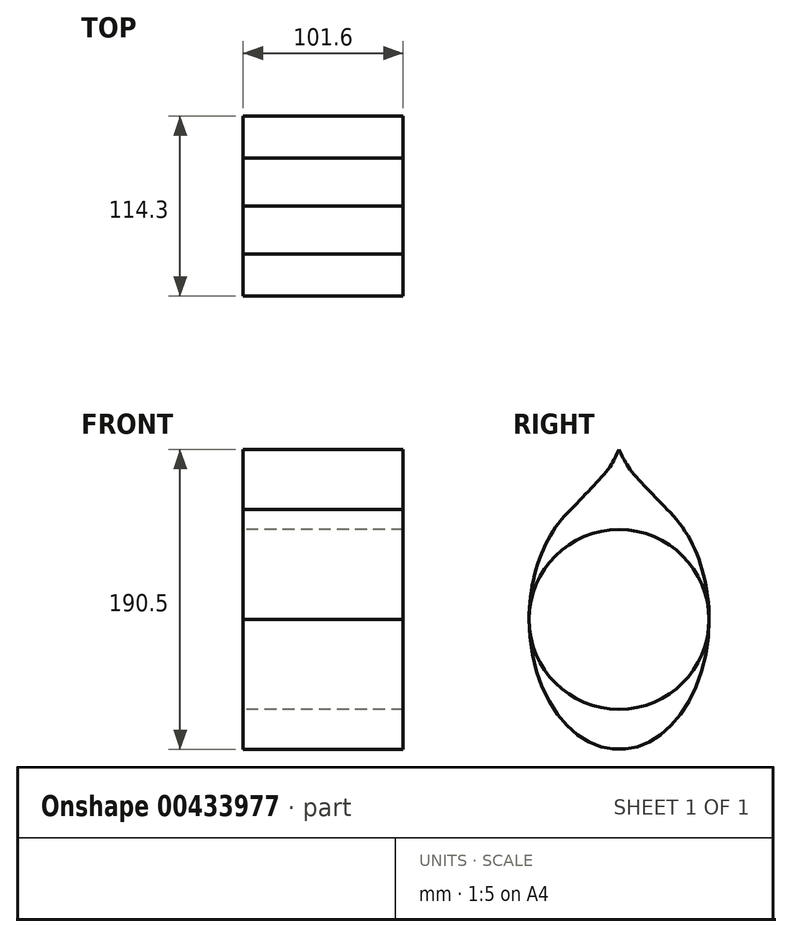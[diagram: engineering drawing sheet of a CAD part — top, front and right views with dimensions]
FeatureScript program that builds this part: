
annotation { "Feature Type Name" : "Feature", "Feature Type Description" : "" }
export const myFeature = defineFeature(function(context is Context, id is Id, definition is map)
    precondition{}
    {
        {
            var Q0;
            Q0=qCreatedBy(makeId("Right.planeOp"),FACE);
            var sketch = newSketch(context, id + "F0", { "sketchPlane" : qUnion([Q0])});
            skCircle(sketch, "E0", {"center": v(0, 0) * mm, "radius": 57.15 * mm});
            skEllipticalArc(sketch, "E1", {});
            skLineSegment(sketch, "E2", {"start": v(0, 82.55) * mm, "end": v(0, 107.95) * mm, "construction": true});
            skLineSegment(sketch, "E3", {"start": v(0, 82.55) * mm, "end": v(0, 57.15) * mm, "construction": true});
            skPoint(sketch, "E4.0.internal.snap0", {"position": v(0, 69.85) * mm});
            skPoint(sketch, "E4.1.internal.snap0", {"position": v(0, 95.25) * mm});
            skFitSpline(sketch, "E4", {"points": [v(30.46, 69.85) * mm, v(7.1, 95.25) * mm, v(0, 107.95) * mm], "startDerivative": vector(-40.1, 45.42) * mm, "endDerivative": vector(-14.34, 29.73) * mm});
            skFitSpline(sketch, "E5.MirrorCS", {"points": [v(-30.46, 69.85) * mm, v(-7.1, 95.25) * mm, v(0, 107.95) * mm], "startDerivative": vector(40.1, 45.42) * mm, "endDerivative": vector(14.34, 29.73) * mm});
            const initialGuessF0  = {"E1": [0, 0, 0, 1, 0.08255, 0.05715, 0.562069803005627, 5.721115504173959]};
            skSetInitialGuess(sketch, initialGuessF0);
            skSolve(sketch);
        }
        {
            var Q0;
            {var subQ0=sQuery(id+"F0.wireOp",EDGE,"E4");Q0=makeQuery(id+"F0.imprint","IMPRINT",FACE,{"disambiguationData":[TD([[makeQuery(id+"F0.imprint","IMPRINT",EDGE,{"derivedFrom":subQ0}),1.0]])]});}
            var Q1;
            {var subQ0=sQuery(id+"F0.wireOp",EDGE,"E1");var subQ1=sQuery(id+"F0.wireOp",EDGE,"E0");var subQ2=makeQuery(id+"F0.imprint","INTERSECT",VERTEX,{"disambiguationData":[OD(0.0)],"derivedFrom":[subQ1,subQ0]});Q1=makeQuery(id+"F0.imprint","IMPRINT",FACE,{"disambiguationData":[TD([[makeQuery(id+"F0.imprint","IMPRINT",EDGE,{"disambiguationData":[TD([[subQ2,-1.0]])],"derivedFrom":subQ1}),-1.0]])]});}
            extrude(context, id + "F1", {"entities" : qUnion([Q0, Q1]), "depth" : 101.6 * mm});
        }
    });
